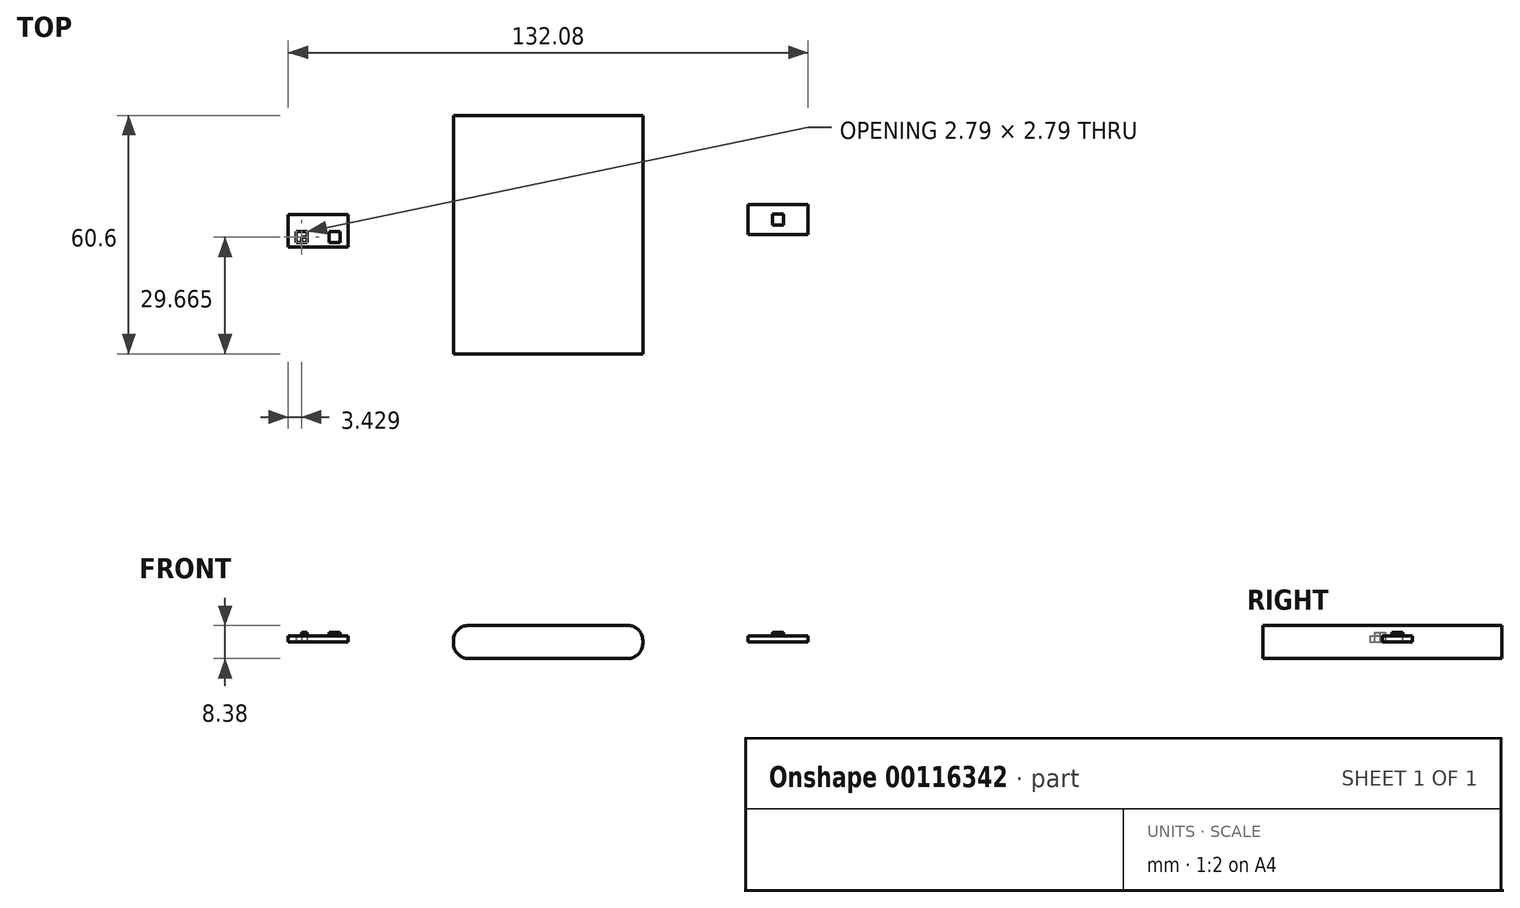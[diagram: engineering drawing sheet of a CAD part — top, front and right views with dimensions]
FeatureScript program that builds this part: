
annotation { "Feature Type Name" : "Feature", "Feature Type Description" : "" }
export const myFeature = defineFeature(function(context is Context, id is Id, definition is map)
    precondition{}
    {
        {
            var Q0;
            Q0=qCreatedBy(makeId("Top.planeOp"),FACE);
            var sketch = newSketch(context, id + "F0", { "sketchPlane" : qUnion([Q0])});
            skLineSegment(sketch, "E0", {"start": v(0, 0) * mm, "end": v(0, 30.3) * mm});
            skLineSegment(sketch, "E1", {"start": v(0, 0) * mm, "end": v(0, -30.3) * mm});
            skLineSegment(sketch, "E2", {"start": v(0, -30.3) * mm, "end": v(-24.05, -30.3) * mm});
            skLineSegment(sketch, "E3", {"start": v(-24.05, -30.3) * mm, "end": v(-24.05, 30.3) * mm});
            skLineSegment(sketch, "E4", {"start": v(-24.05, 30.3) * mm, "end": v(24.05, 30.3) * mm});
            skLineSegment(sketch, "E5", {"start": v(24.05, 30.3) * mm, "end": v(24.05, -30.3) * mm});
            skLineSegment(sketch, "E6", {"start": v(24.05, -30.3) * mm, "end": v(0, -30.3) * mm});
            skSolve(sketch);
        }
        {
            var Q0;
            {var subQ1=sQuery(id+"F0.wireOp",EDGE,"E0");Q0=makeQuery(id+"F0.imprint","IMPRINT",FACE,{"disambiguationData":[TD([[makeQuery(id+"F0.imprint","IMPRINT",EDGE,{"derivedFrom":subQ1}),1.0]])]});}
            var Q1;
            {var subQ2=sQuery(id+"F0.wireOp",EDGE,"E0");Q1=makeQuery(id+"F0.imprint","IMPRINT",FACE,{"disambiguationData":[TD([[makeQuery(id+"F0.imprint","IMPRINT",EDGE,{"derivedFrom":subQ2}),-1.0]])]});}
            extrude(context, id + "F1", {"entities" : qUnion([Q0, Q1]), "depth" : 8.38 * mm, "offsetDistance" : 25.4 * mm, "symmetric" : true});
        }
        {
            var Q0;
            Q0=qCreatedBy(makeId("Top.planeOp"),FACE);
            var sketch = newSketch(context, id + "F2", { "sketchPlane" : qUnion([Q0])});
            skLineSegment(sketch, "E7", {"start": v(0, 0) * mm, "end": v(-50.8, 0) * mm});
            skLineSegment(sketch, "E8", {"start": v(-50.8, 0) * mm, "end": v(-50.8, 5.08) * mm});
            skLineSegment(sketch, "E9", {"start": v(-66.04, 5.08) * mm, "end": v(-66.04, -3.18) * mm});
            skLineSegment(sketch, "E10", {"start": v(-66.04, -3.18) * mm, "end": v(-50.8, -3.18) * mm});
            skLineSegment(sketch, "E11", {"start": v(-50.8, -3.18) * mm, "end": v(-50.8, 0) * mm});
            skLineSegment(sketch, "E12", {"start": v(-50.8, 0) * mm, "end": v(-62.61, 0) * mm});
            skLineSegment(sketch, "E13", {"start": v(-50.8, 0) * mm, "end": v(-54.23, 0) * mm});
            skLineSegment(sketch, "E14", {"start": v(-62.61, -3.18) * mm, "end": v(-62.61, -0.64) * mm});
            skLineSegment(sketch, "E15", {"start": v(-62.61, -0.64) * mm, "end": v(-54.23, -0.64) * mm});
            skLineSegment(sketch, "E16.bottom", {"start": v(-61.21, -2.03) * mm, "end": v(-64, -2.03) * mm});
            skLineSegment(sketch, "E16.top", {"start": v(-61.21, 0.76) * mm, "end": v(-64, 0.76) * mm});
            skLineSegment(sketch, "E16.left", {"start": v(-61.21, -2.03) * mm, "end": v(-61.21, 0.76) * mm});
            skLineSegment(sketch, "E16.right", {"start": v(-64, -2.03) * mm, "end": v(-64, 0.76) * mm});
            skPoint(sketch, "E16.middle", {"position": v(-62.61, -0.64) * mm});
            skLineSegment(sketch, "E17.bottom", {"start": v(-52.83, -2.03) * mm, "end": v(-55.63, -2.03) * mm});
            skLineSegment(sketch, "E17.top", {"start": v(-52.83, 0.76) * mm, "end": v(-55.63, 0.76) * mm});
            skLineSegment(sketch, "E17.left", {"start": v(-52.83, -2.03) * mm, "end": v(-52.83, 0.76) * mm});
            skLineSegment(sketch, "E17.right", {"start": v(-55.63, -2.03) * mm, "end": v(-55.63, 0.76) * mm});
            skPoint(sketch, "E17.middle", {"position": v(-54.23, -0.64) * mm});
            skLineSegment(sketch, "E18", {"start": v(-66.04, 5.08) * mm, "end": v(-50.8, 5.08) * mm});
            skSolve(sketch);
        }
        {
            var Q0;
            {var subQ11=sQuery(id+"F2.wireOp",EDGE,"E8");Q0=makeQuery(id+"F2.imprint","IMPRINT",FACE,{"disambiguationData":[TD([[makeQuery(id+"F2.imprint","IMPRINT",EDGE,{"derivedFrom":subQ11}),1.0]])]});}
            var Q1;
            {var subQ1=sQuery(id+"F2.wireOp",EDGE,"E11");Q1=makeQuery(id+"F2.imprint","IMPRINT",FACE,{"disambiguationData":[TD([[makeQuery(id+"F2.imprint","IMPRINT",EDGE,{"derivedFrom":subQ1}),1.0]])]});}
            var Q2;
            {var subQ0=sQuery(id+"F2.wireOp",EDGE,"E16.left");var subQ1=sQuery(id+"F2.wireOp",EDGE,"E12");var subQ2=makeQuery(id+"F2.imprint","INTERSECT",VERTEX,{"derivedFrom":[subQ1,subQ0]});Q2=makeQuery(id+"F2.imprint","IMPRINT",FACE,{"disambiguationData":[TD([[makeQuery(id+"F2.imprint","IMPRINT",EDGE,{"disambiguationData":[TD([[subQ2,1.0]])],"derivedFrom":subQ1}),1.0]])]});}
            var Q3;
            {var subQ8=sQuery(id+"F2.wireOp",EDGE,"E16.top");Q3=makeQuery(id+"F2.imprint","IMPRINT",FACE,{"disambiguationData":[TD([[makeQuery(id+"F2.imprint","IMPRINT",EDGE,{"derivedFrom":subQ8}),1.0]])]});}
            var Q4;
            {var subQ1=sQuery(id+"F2.wireOp",EDGE,"E17.bottom");Q4=makeQuery(id+"F2.imprint","IMPRINT",FACE,{"disambiguationData":[TD([[makeQuery(id+"F2.imprint","IMPRINT",EDGE,{"derivedFrom":subQ1}),-1.0]])]});}
            var Q5;
            {var subQ0=sQuery(id+"F2.wireOp",EDGE,"E15");var subQ1=sQuery(id+"F2.wireOp",EDGE,"E14");var subQ2=makeQuery(id+"F2.imprint","INTERSECT",VERTEX,{"derivedFrom":[subQ1,subQ0]});Q5=makeQuery(id+"F2.imprint","IMPRINT",FACE,{"disambiguationData":[TD([[makeQuery(id+"F2.imprint","IMPRINT",EDGE,{"disambiguationData":[TD([[subQ2,1.0]])],"derivedFrom":subQ1}),-1.0]])]});}
            var Q6;
            {var subQ0=sQuery(id+"F2.wireOp",EDGE,"E17.top");Q6=makeQuery(id+"F2.imprint","IMPRINT",FACE,{"disambiguationData":[TD([[makeQuery(id+"F2.imprint","IMPRINT",EDGE,{"derivedFrom":subQ0}),1.0]])]});}
            extrude(context, id + "F3", {"entities" : qUnion([Q0, Q1, Q2, Q3, Q4, Q5, Q6]), "depth" : 1.57 * mm, "offsetDistance" : 25.4 * mm});
        }
        {
            var Q0;
            {var subQ8=sQuery(id+"F2.wireOp",EDGE,"E16.top");Q0=makeQuery(id+"F2.imprint","IMPRINT",FACE,{"disambiguationData":[TD([[makeQuery(id+"F2.imprint","IMPRINT",EDGE,{"derivedFrom":subQ8}),1.0]])]});}
            var Q1;
            {var subQ0=sQuery(id+"F2.wireOp",EDGE,"E15");var subQ1=sQuery(id+"F2.wireOp",EDGE,"E14");var subQ2=makeQuery(id+"F2.imprint","INTERSECT",VERTEX,{"derivedFrom":[subQ1,subQ0]});Q1=makeQuery(id+"F2.imprint","IMPRINT",FACE,{"disambiguationData":[TD([[makeQuery(id+"F2.imprint","IMPRINT",EDGE,{"disambiguationData":[TD([[subQ2,1.0]])],"derivedFrom":subQ1}),-1.0]])]});}
            var Q2;
            {var subQ1=sQuery(id+"F2.wireOp",EDGE,"E17.bottom");Q2=makeQuery(id+"F2.imprint","IMPRINT",FACE,{"disambiguationData":[TD([[makeQuery(id+"F2.imprint","IMPRINT",EDGE,{"derivedFrom":subQ1}),-1.0]])]});}
            var Q3;
            {var subQ0=sQuery(id+"F2.wireOp",EDGE,"E17.top");Q3=makeQuery(id+"F2.imprint","IMPRINT",FACE,{"disambiguationData":[TD([[makeQuery(id+"F2.imprint","IMPRINT",EDGE,{"derivedFrom":subQ0}),1.0]])]});}
            extrude(context, id + "F4", {"entities" : qUnion([Q0, Q1, Q2, Q3]), "operationType" : NewBodyOperationType.ADD, "depth" : 2.4 * mm, "offsetDistance" : 25.4 * mm});
        }
        {
            var Q0;
            Q0=qCreatedBy(makeId("Top.planeOp"),FACE);
            var sketch = newSketch(context, id + "F5", { "sketchPlane" : qUnion([Q0])});
            skLineSegment(sketch, "E19", {"start": v(0, 0) * mm, "end": v(50.8, 0) * mm});
            skLineSegment(sketch, "E20", {"start": v(50.8, 0) * mm, "end": v(50.8, 7.62) * mm});
            skLineSegment(sketch, "E21", {"start": v(50.8, 7.62) * mm, "end": v(66.04, 7.62) * mm});
            skLineSegment(sketch, "E22", {"start": v(66.04, 7.62) * mm, "end": v(66.04, 0) * mm});
            skLineSegment(sketch, "E23", {"start": v(66.04, 0) * mm, "end": v(50.8, 0) * mm});
            skLineSegment(sketch, "E24", {"start": v(58.42, 0) * mm, "end": v(58.42, 3.81) * mm});
            skPoint(sketch, "E24.endSnap0", {"position": v(66.04, 3.81) * mm});
            skLineSegment(sketch, "E25.bottom", {"start": v(59.82, 2.41) * mm, "end": v(57.02, 2.41) * mm});
            skLineSegment(sketch, "E25.top", {"start": v(59.82, 5.2) * mm, "end": v(57.02, 5.2) * mm});
            skLineSegment(sketch, "E25.left", {"start": v(59.82, 2.41) * mm, "end": v(59.82, 5.2) * mm});
            skLineSegment(sketch, "E25.right", {"start": v(57.02, 2.41) * mm, "end": v(57.02, 5.2) * mm});
            skPoint(sketch, "E25.middle", {"position": v(58.42, 3.81) * mm});
            skSolve(sketch);
        }
        {
            var Q0;
            {var subQ3=sQuery(id+"F5.wireOp",EDGE,"E20");Q0=makeQuery(id+"F5.imprint","IMPRINT",FACE,{"disambiguationData":[TD([[makeQuery(id+"F5.imprint","IMPRINT",EDGE,{"derivedFrom":subQ3}),-1.0]])]});}
            var Q1;
            Q1=makeQuery(id+"F5.imprint","IMPRINT",FACE,{"disambiguationData":[TD([[makeQuery(id+"F5.imprint","IMPRINT",EDGE,{"derivedFrom":sQuery(id+"F5.wireOp",EDGE,"E25.top")}),1.0]])]});
            extrude(context, id + "F6", {"entities" : qUnion([Q0, Q1]), "depth" : 1.57 * mm, "offsetDistance" : 25.4 * mm});
        }
        {
            var Q0;
            Q0=makeQuery(id+"F5.imprint","IMPRINT",FACE,{"disambiguationData":[TD([[makeQuery(id+"F5.imprint","IMPRINT",EDGE,{"derivedFrom":sQuery(id+"F5.wireOp",EDGE,"E25.top")}),1.0]])]});
            extrude(context, id + "F7", {"entities" : qUnion([Q0]), "operationType" : NewBodyOperationType.ADD, "depth" : 2.4 * mm, "offsetDistance" : 25.4 * mm});
        }
        {
            var Q0;
            Q0=makeQuery(id+"F1.opExtrude","CAP_EDGE",EDGE,{"disambiguationData":[OSD([sQuery(id+"F0.wireOp",EDGE,"E3")])],"isStart":false});
            var Q1;
            Q1=makeQuery(id+"F1.opExtrude","CAP_EDGE",EDGE,{"disambiguationData":[OSD([sQuery(id+"F0.wireOp",EDGE,"E3")])],"isStart":true});
            var Q2;
            Q2=makeQuery(id+"F1.opExtrude","CAP_EDGE",EDGE,{"disambiguationData":[OSD([sQuery(id+"F0.wireOp",EDGE,"E5")])],"isStart":false});
            var Q3;
            Q3=makeQuery(id+"F1.opExtrude","CAP_EDGE",EDGE,{"disambiguationData":[OSD([sQuery(id+"F0.wireOp",EDGE,"E5")])],"isStart":true});
            fillet(context, id + "F8", {"entities" : qUnion([Q0, Q1, Q2, Q3]), "radius" : 3.8 * mm, "tangentPropagation" : true, "allowEdgeOverflow" : false});
        }
    });
